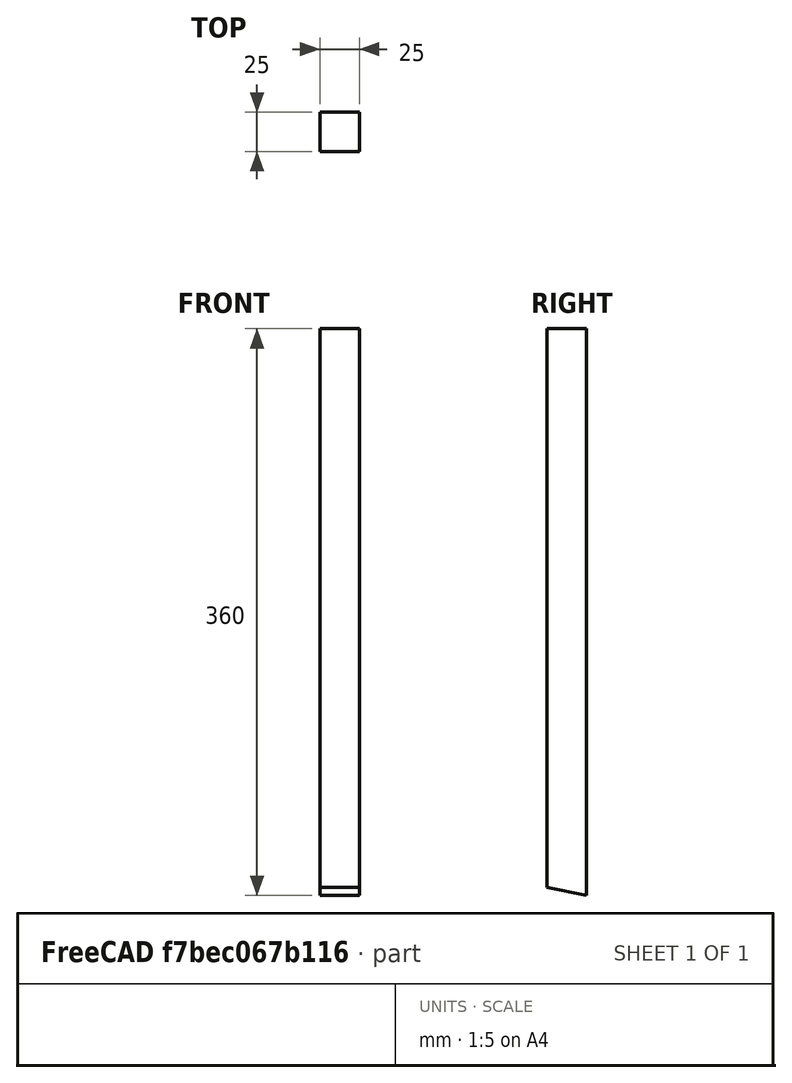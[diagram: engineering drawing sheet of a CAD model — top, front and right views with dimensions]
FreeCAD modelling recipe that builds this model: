
FCSTD DOCUMENT  (FreeCAD 0.19R24366 (Git))
Label: Part4Hollow
License: All rights reserved
LicenseURL: http://en.wikipedia.org/wiki/All_rights_reserved
objects: TechDraw::DrawViewDimension×4, Sketcher::SketchObject×1, PartDesign::Pad×1, PartDesign::Body×1, TechDraw::DrawSVGTemplate×1, TechDraw::DrawViewPart×1, TechDraw::DrawPage×1
note: 4 computed .brp shape members not serialized (recipe doc carries the construction recipe); baked Part::Feature solids carry a one-line shape summary decoded from their .brp

FEATURE [Sketcher::SketchObject] Sketch
  FullyConstrained = true
  MapMode = 5
  Placement = pos=(0,0,0) rot=(0.57735,0.57735,0.57735;2.0944rad)
  Support = -> [YZ_Plane]
  sketch-geometry (4):
    g0: LineSegment StartX=-12.5 StartY=180 StartZ=0 EndX=12.5 EndY=180 EndZ=0
    g1: LineSegment StartX=12.5 StartY=180 StartZ=0 EndX=12.5 EndY=-180 EndZ=0
    g2: LineSegment StartX=12.5 StartY=-180 StartZ=0 EndX=-12.5 EndY=-175 EndZ=0
    g3: LineSegment StartX=-12.5 StartY=-175 StartZ=0 EndX=-12.5 EndY=180 EndZ=0
  constraints (12):
    c: Coincident(g0,g1)
    c: Coincident(g1,g2)
    c: Coincident(g2,g3)
    c: Coincident(g3,g0)
    c: Horizontal(g0)
    c: Vertical(g1)
    c: Vertical(g3)
    c: DistanceY(g1,g1) = 360
    c: DistanceX(g0,g0) = 25
    c: DistanceY(g2,g0) = 355
    c: DistanceY(g-1,g0) = 180
    c: DistanceX(g0,g-1) = 12.5
FEATURE [PartDesign::Pad] Pad
  Direction = (1,1,1)
  Length = 25
  Length2 = 100
  Placement = pos=(0,0,0) rot=(0.57735,0.57735,0.57735;2.0944rad)
  Profile = -> Sketch
  Type = 0
FEATURE [PartDesign::Body] Body
  Group = -> [Sketch,Pad]
  Origin = -> Origin
  Tip = -> Pad
FEATURE [TechDraw::DrawSVGTemplate] Template
  EditableTexts = AUTHOR_NAME=Natan Hari Pamungkas; DN=Part - 03; DRAWING_TITLE=Part Besi Hollow - 03; FC-DATE=18/03/2022; FC-REV=REV A; FC-SC=0.5; FC-SH=X / Y; FC-SI=A4; FreeCAD_DRAWING=Jumlah item 2; PN=Hollow - 03; SI-1=Besi Hollow Ukuran 2.5 cm x 2.5 cm; SI-2=Ketebalan menyesuaikan
  Height = 297
  Orientation = 0
  Width = 210
FEATURE [TechDraw::DrawViewPart] View  label="Right"
  CoarseView = false
  Direction = (1,0,0)
  Focus = 100
  HardHidden = false
  IsoCount = 0
  IsoHidden = false
  IsoVisible = false
  LockPosition = false
  Perspective = false
  Rotation = 0
  Scale = 0.5
  ScaleType = 0
  SeamHidden = false
  SeamVisible = true
  SmoothHidden = false
  SmoothVisible = true
  Source = -> [Body]
  X = 106.05
  XDirection = (0,1,0)
  Y = 184.76
FEATURE [TechDraw::DrawViewDimension] Dimension
  Arbitrary = false
  ArbitraryTolerances = false
  EqualTolerance = true
  FormatSpec = %.2f
  FormatSpecOverTolerance = %+.2f
  FormatSpecUnderTolerance = %+.2f
  Inverted = false
  LockPosition = false
  MeasureType = 1
  OverTolerance = 0
  References2D = -> [View]
  Rotation = 0
  ScaleType = 0
  TheoreticalExact = false
  Type = 1
  UnderTolerance = 0
  X = 0
  Y = 99.4488
FEATURE [TechDraw::DrawViewDimension] Dimension001
  Arbitrary = false
  ArbitraryTolerances = false
  EqualTolerance = true
  FormatSpec = %.2f
  FormatSpecOverTolerance = %+.2f
  FormatSpecUnderTolerance = %+.2f
  Inverted = false
  LockPosition = false
  MeasureType = 1
  OverTolerance = 0
  References2D = -> [View]
  Rotation = 0
  ScaleType = 0
  TheoreticalExact = false
  Type = 2
  UnderTolerance = 0
  X = 21.1549
  Y = -0.784469
FEATURE [TechDraw::DrawViewDimension] Dimension002
  Arbitrary = false
  ArbitraryTolerances = false
  EqualTolerance = true
  FormatSpec = %.2f
  FormatSpecOverTolerance = %+.2f
  FormatSpecUnderTolerance = %+.2f
  Inverted = false
  LockPosition = false
  MeasureType = 1
  OverTolerance = 0
  References2D = -> [View]
  Rotation = 0
  ScaleType = 0
  TheoreticalExact = false
  Type = 2
  UnderTolerance = 0
  X = -19.586
  Y = -1.10341
FEATURE [TechDraw::DrawViewDimension] Dimension003
  Arbitrary = false
  ArbitraryTolerances = false
  EqualTolerance = true
  FormatSpec = %.2f
  FormatSpecOverTolerance = %+.2f
  FormatSpecUnderTolerance = %+.2f
  Inverted = false
  LockPosition = false
  MeasureType = 1
  OverTolerance = 0
  References2D = -> [View]
  Rotation = 0
  ScaleType = 0
  TheoreticalExact = false
  Type = 0
  UnderTolerance = 0
  X = -5.09905
  Y = -99.3403
FEATURE [TechDraw::DrawPage] Page
  KeepUpdated = true
  NextBalloonIndex = 1
  ProjectionType = 0
  Template = -> Template
  Views = -> [View,Dimension,Dimension001,Dimension002,Dimension003]
